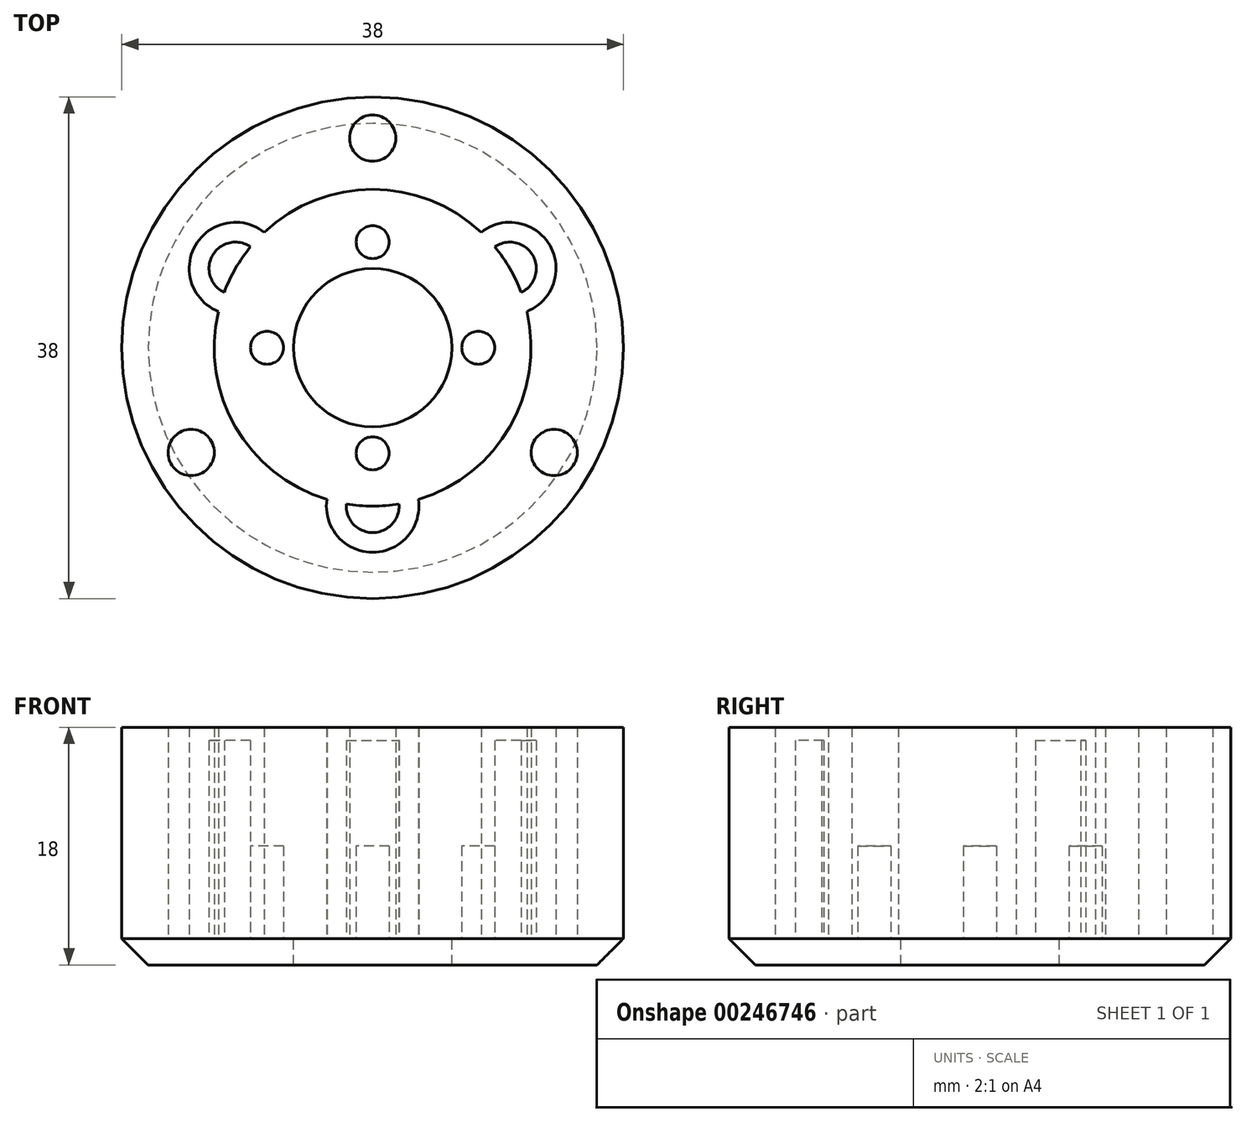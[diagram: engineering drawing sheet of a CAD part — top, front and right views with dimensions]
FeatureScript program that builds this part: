
annotation { "Feature Type Name" : "Feature", "Feature Type Description" : "" }
export const myFeature = defineFeature(function(context is Context, id is Id, definition is map)
    precondition{}
    {
        {
            var Q0;
            Q0=qCreatedBy(makeId("Top.planeOp"),FACE);
            var sketch = newSketch(context, id + "F0", { "sketchPlane" : qUnion([Q0])});
            skCircle(sketch, "E0", {"center": v(0, 0) * mm, "radius": 12 * mm});
            skCircle(sketch, "E1", {"center": v(0, 0) * mm, "radius": 8 * mm, "construction": true});
            skLineSegment(sketch, "E2", {"start": v(0, 34.6) * mm, "end": v(0, -37) * mm, "construction": true});
            skLineSegment(sketch, "E3", {"start": v(36.08, 20.83) * mm, "end": v(-44.46, -25.67) * mm, "construction": true});
            skLineSegment(sketch, "E4", {"start": v(-38.88, 22.45) * mm, "end": v(53.4, -30.83) * mm, "construction": true});
            skCircle(sketch, "E5", {"center": v(-10.4, 6) * mm, "radius": 3.5 * mm});
            skCircle(sketch, "E6", {"center": v(10.4, 6) * mm, "radius": 3.5 * mm});
            skCircle(sketch, "E7", {"center": v(0, -12) * mm, "radius": 3.5 * mm});
            skCircle(sketch, "E8", {"center": v(0, 0) * mm, "radius": 19 * mm});
            skCircle(sketch, "E9", {"center": v(0, 0) * mm, "radius": 15.88 * mm, "construction": true});
            skCircle(sketch, "E10", {"center": v(-13.75, -7.94) * mm, "radius": 1.75 * mm});
            skCircle(sketch, "E11", {"center": v(13.75, -7.94) * mm, "radius": 1.75 * mm});
            skCircle(sketch, "E12", {"center": v(0, 15.88) * mm, "radius": 1.75 * mm});
            skCircle(sketch, "E13", {"center": v(-10.4, 6) * mm, "radius": 2 * mm});
            skCircle(sketch, "E14", {"center": v(10.4, 6) * mm, "radius": 2 * mm});
            skCircle(sketch, "E15", {"center": v(0, -12) * mm, "radius": 2 * mm});
            skCircle(sketch, "E16", {"center": v(0, 0) * mm, "radius": 6 * mm});
            skCircle(sketch, "E17", {"center": v(0, 8) * mm, "radius": 1.25 * mm});
            skCircle(sketch, "E18", {"center": v(8, 0) * mm, "radius": 1.25 * mm});
            skCircle(sketch, "E19", {"center": v(-8, 0) * mm, "radius": 1.25 * mm});
            skCircle(sketch, "E20", {"center": v(0, -8) * mm, "radius": 1.25 * mm});
            skSolve(sketch);
        }
        {
            var Q0;
            Q0=makeQuery(id+"F0.imprint","IMPRINT",FACE,{"disambiguationData":[TD([[makeQuery(id+"F0.imprint","IMPRINT",EDGE,{"derivedFrom":sQuery(id+"F0.wireOp",EDGE,"E8")}),1.0]])]});
            extrude(context, id + "F1", {"entities" : qUnion([Q0]), "depth" : 16 * mm});
        }
        {
            var Q0;
            Q0=makeQuery(id+"F0.imprint","IMPRINT",FACE,{"disambiguationData":[TD([[makeQuery(id+"F0.imprint","IMPRINT",EDGE,{"derivedFrom":sQuery(id+"F0.wireOp",EDGE,"E10")}),1.0]])]});
            var Q1;
            {var subQ0=sQuery(id+"F0.wireOp",EDGE,"E14");var subQ1=sQuery(id+"F0.wireOp",EDGE,"E0");var subQ2=makeQuery(id+"F0.imprint","INTERSECT",VERTEX,{"disambiguationData":[OD(0.0)],"derivedFrom":[subQ1,subQ0]});Q1=makeQuery(id+"F0.imprint","IMPRINT",FACE,{"disambiguationData":[TD([[makeQuery(id+"F0.imprint","IMPRINT",EDGE,{"disambiguationData":[TD([[subQ2,1.0]])],"derivedFrom":subQ1}),-1.0]])]});}
            var Q2;
            {var subQ0=sQuery(id+"F0.wireOp",EDGE,"E14");var subQ1=sQuery(id+"F0.wireOp",EDGE,"E0");var subQ2=makeQuery(id+"F0.imprint","INTERSECT",VERTEX,{"disambiguationData":[OD(0.0)],"derivedFrom":[subQ1,subQ0]});Q2=makeQuery(id+"F0.imprint","IMPRINT",FACE,{"disambiguationData":[TD([[makeQuery(id+"F0.imprint","IMPRINT",EDGE,{"disambiguationData":[TD([[subQ2,1.0]])],"derivedFrom":subQ1}),1.0]])]});}
            var Q3;
            {var subQ0=sQuery(id+"F0.wireOp",EDGE,"E7");var subQ1=sQuery(id+"F0.wireOp",EDGE,"E0");var subQ7=makeQuery(id+"F0.imprint","INTERSECT",VERTEX,{"disambiguationData":[OD(0.0)],"derivedFrom":[subQ1,subQ0]});Q3=makeQuery(id+"F0.imprint","IMPRINT",FACE,{"disambiguationData":[TD([[makeQuery(id+"F0.imprint","IMPRINT",EDGE,{"disambiguationData":[TD([[subQ7,-1.0]])],"derivedFrom":subQ1}),1.0]])]});}
            var Q4;
            Q4=makeQuery(id+"F0.imprint","IMPRINT",FACE,{"disambiguationData":[TD([[makeQuery(id+"F0.imprint","IMPRINT",EDGE,{"derivedFrom":sQuery(id+"F0.wireOp",EDGE,"E16")}),-1.0]])]});
            var Q5;
            {var subQ0=sQuery(id+"F0.wireOp",EDGE,"E7");var subQ1=sQuery(id+"F0.wireOp",EDGE,"E0");var subQ2=makeQuery(id+"F0.imprint","INTERSECT",VERTEX,{"disambiguationData":[OD(0.0)],"derivedFrom":[subQ1,subQ0]});Q5=makeQuery(id+"F0.imprint","IMPRINT",FACE,{"disambiguationData":[TD([[makeQuery(id+"F0.imprint","IMPRINT",EDGE,{"disambiguationData":[TD([[subQ2,-1.0]])],"derivedFrom":subQ1}),-1.0]])]});}
            var Q6;
            Q6=makeQuery(id+"F0.imprint","IMPRINT",FACE,{"disambiguationData":[TD([[makeQuery(id+"F0.imprint","IMPRINT",EDGE,{"derivedFrom":sQuery(id+"F0.wireOp",EDGE,"E11")}),1.0]])]});
            var Q7;
            Q7=makeQuery(id+"F0.imprint","IMPRINT",FACE,{"disambiguationData":[TD([[makeQuery(id+"F0.imprint","IMPRINT",EDGE,{"derivedFrom":sQuery(id+"F0.wireOp",EDGE,"E12")}),1.0]])]});
            var Q8;
            {var subQ0=sQuery(id+"F0.wireOp",EDGE,"E14");var subQ1=sQuery(id+"F0.wireOp",EDGE,"E0");var subQ2=makeQuery(id+"F0.imprint","INTERSECT",VERTEX,{"disambiguationData":[OD(0.0)],"derivedFrom":[subQ1,subQ0]});Q8=makeQuery(id+"F0.imprint","IMPRINT",FACE,{"disambiguationData":[TD([[makeQuery(id+"F0.imprint","IMPRINT",EDGE,{"disambiguationData":[TD([[subQ2,-1.0]])],"derivedFrom":subQ1}),1.0]])]});}
            var Q9;
            {var subQ0=sQuery(id+"F0.wireOp",EDGE,"E14");var subQ1=sQuery(id+"F0.wireOp",EDGE,"E0");var subQ2=makeQuery(id+"F0.imprint","INTERSECT",VERTEX,{"disambiguationData":[OD(0.0)],"derivedFrom":[subQ1,subQ0]});Q9=makeQuery(id+"F0.imprint","IMPRINT",FACE,{"disambiguationData":[TD([[makeQuery(id+"F0.imprint","IMPRINT",EDGE,{"disambiguationData":[TD([[subQ2,-1.0]])],"derivedFrom":subQ1}),-1.0]])]});}
            var Q10;
            {var subQ0=sQuery(id+"F0.wireOp",EDGE,"E13");var subQ1=sQuery(id+"F0.wireOp",EDGE,"E0");var subQ2=makeQuery(id+"F0.imprint","INTERSECT",VERTEX,{"disambiguationData":[OD(0.0)],"derivedFrom":[subQ1,subQ0]});Q10=makeQuery(id+"F0.imprint","IMPRINT",FACE,{"disambiguationData":[TD([[makeQuery(id+"F0.imprint","IMPRINT",EDGE,{"disambiguationData":[TD([[subQ2,-1.0]])],"derivedFrom":subQ1}),-1.0]])]});}
            var Q11;
            {var subQ0=sQuery(id+"F0.wireOp",EDGE,"E13");var subQ1=sQuery(id+"F0.wireOp",EDGE,"E0");var subQ2=makeQuery(id+"F0.imprint","INTERSECT",VERTEX,{"disambiguationData":[OD(0.0)],"derivedFrom":[subQ1,subQ0]});Q11=makeQuery(id+"F0.imprint","IMPRINT",FACE,{"disambiguationData":[TD([[makeQuery(id+"F0.imprint","IMPRINT",EDGE,{"disambiguationData":[TD([[subQ2,-1.0]])],"derivedFrom":subQ1}),1.0]])]});}
            var Q12;
            {var subQ0=sQuery(id+"F0.wireOp",EDGE,"E15");var subQ1=sQuery(id+"F0.wireOp",EDGE,"E0");var subQ2=makeQuery(id+"F0.imprint","INTERSECT",VERTEX,{"disambiguationData":[OD(0.0)],"derivedFrom":[subQ1,subQ0]});Q12=makeQuery(id+"F0.imprint","IMPRINT",FACE,{"disambiguationData":[TD([[makeQuery(id+"F0.imprint","IMPRINT",EDGE,{"disambiguationData":[TD([[subQ2,-1.0]])],"derivedFrom":subQ1}),1.0]])]});}
            var Q13;
            {var subQ0=sQuery(id+"F0.wireOp",EDGE,"E15");var subQ1=sQuery(id+"F0.wireOp",EDGE,"E0");var subQ2=makeQuery(id+"F0.imprint","INTERSECT",VERTEX,{"disambiguationData":[OD(0.0)],"derivedFrom":[subQ1,subQ0]});Q13=makeQuery(id+"F0.imprint","IMPRINT",FACE,{"disambiguationData":[TD([[makeQuery(id+"F0.imprint","IMPRINT",EDGE,{"disambiguationData":[TD([[subQ2,-1.0]])],"derivedFrom":subQ1}),-1.0]])]});}
            var Q14;
            Q14=makeQuery(id+"F0.imprint","IMPRINT",FACE,{"disambiguationData":[TD([[makeQuery(id+"F0.imprint","IMPRINT",EDGE,{"derivedFrom":sQuery(id+"F0.wireOp",EDGE,"E8")}),1.0]])]});
            var Q15;
            {var subQ0=sQuery(id+"F0.wireOp",EDGE,"E5");var subQ1=sQuery(id+"F0.wireOp",EDGE,"E0");var subQ2=makeQuery(id+"F0.imprint","INTERSECT",VERTEX,{"disambiguationData":[OD(0.0)],"derivedFrom":[subQ1,subQ0]});Q15=makeQuery(id+"F0.imprint","IMPRINT",FACE,{"disambiguationData":[TD([[makeQuery(id+"F0.imprint","IMPRINT",EDGE,{"disambiguationData":[TD([[subQ2,-1.0]])],"derivedFrom":subQ1}),-1.0]])]});}
            var Q16;
            {var subQ0=sQuery(id+"F0.wireOp",EDGE,"E5");var subQ1=sQuery(id+"F0.wireOp",EDGE,"E0");var subQ2=makeQuery(id+"F0.imprint","INTERSECT",VERTEX,{"disambiguationData":[OD(0.0)],"derivedFrom":[subQ1,subQ0]});Q16=makeQuery(id+"F0.imprint","IMPRINT",FACE,{"disambiguationData":[TD([[makeQuery(id+"F0.imprint","IMPRINT",EDGE,{"disambiguationData":[TD([[subQ2,-1.0]])],"derivedFrom":subQ1}),1.0]])]});}
            var Q17;
            Q17=makeQuery(id+"F1.opExtrude","CAP_FACE",FACE,{"disambiguationData":[OSD([sQuery(id+"F0.wireOp",EDGE,"E0"),sQuery(id+"F0.wireOp",EDGE,"E5"),sQuery(id+"F0.wireOp",EDGE,"E6"),sQuery(id+"F0.wireOp",EDGE,"E7"),sQuery(id+"F0.wireOp",EDGE,"E8"),sQuery(id+"F0.wireOp",EDGE,"E10"),sQuery(id+"F0.wireOp",EDGE,"E11"),sQuery(id+"F0.wireOp",EDGE,"E12")])],"isStart":true});
            var Q18;
            {var subQ0=sQuery(id+"F0.wireOp",EDGE,"E20");var subQ1=sQuery(id+"F0.wireOp",EDGE,"E7");var subQ2=makeQuery(id+"F0.imprint","INTERSECT",VERTEX,{"disambiguationData":[OD(0.0)],"derivedFrom":[subQ1,subQ0]});Q18=makeQuery(id+"F0.imprint","IMPRINT",FACE,{"disambiguationData":[TD([[makeQuery(id+"F0.imprint","IMPRINT",EDGE,{"disambiguationData":[TD([[subQ2,-1.0]])],"derivedFrom":subQ1}),-1.0]])]});}
            var Q19;
            Q19=makeQuery(id+"F0.imprint","IMPRINT",FACE,{"disambiguationData":[TD([[makeQuery(id+"F0.imprint","IMPRINT",EDGE,{"derivedFrom":sQuery(id+"F0.wireOp",EDGE,"E17")}),1.0]])]});
            var Q20;
            Q20=makeQuery(id+"F0.imprint","IMPRINT",FACE,{"disambiguationData":[TD([[makeQuery(id+"F0.imprint","IMPRINT",EDGE,{"derivedFrom":sQuery(id+"F0.wireOp",EDGE,"E18")}),1.0]])]});
            var Q21;
            Q21=makeQuery(id+"F0.imprint","IMPRINT",FACE,{"disambiguationData":[TD([[makeQuery(id+"F0.imprint","IMPRINT",EDGE,{"derivedFrom":sQuery(id+"F0.wireOp",EDGE,"E19")}),1.0]])]});
            var Q22;
            Q22=makeQuery(id+"F1.opExtrude","CAP_FACE",FACE,{"disambiguationData":[OSD([sQuery(id+"F0.wireOp",EDGE,"E0"),sQuery(id+"F0.wireOp",EDGE,"E5"),sQuery(id+"F0.wireOp",EDGE,"E6"),sQuery(id+"F0.wireOp",EDGE,"E7"),sQuery(id+"F0.wireOp",EDGE,"E8"),sQuery(id+"F0.wireOp",EDGE,"E10"),sQuery(id+"F0.wireOp",EDGE,"E11"),sQuery(id+"F0.wireOp",EDGE,"E12")])],"isStart":false});
            var Q23;
            {var subQ0=sQuery(id+"F0.wireOp",EDGE,"E20");var subQ1=sQuery(id+"F0.wireOp",EDGE,"E7");var subQ2=makeQuery(id+"F0.imprint","INTERSECT",VERTEX,{"disambiguationData":[OD(0.0)],"derivedFrom":[subQ1,subQ0]});Q23=makeQuery(id+"F0.imprint","IMPRINT",FACE,{"disambiguationData":[TD([[makeQuery(id+"F0.imprint","IMPRINT",EDGE,{"disambiguationData":[TD([[subQ2,-1.0]])],"derivedFrom":subQ1}),1.0]])]});}
            extrude(context, id + "F2", {"entities" : qUnion([Q0, Q1, Q2, Q3, Q4, Q5, Q6, Q7, Q8, Q9, Q10, Q11, Q12, Q13, Q14, Q15, Q16, Q17, Q18, Q19, Q20, Q21, Q22, Q23]), "operationType" : NewBodyOperationType.ADD, "oppositeDirection" : true, "depth" : 2 * mm});
        }
        {
            var Q0;
            Q0=makeQuery(id+"F0.imprint","IMPRINT",FACE,{"disambiguationData":[TD([[makeQuery(id+"F0.imprint","IMPRINT",EDGE,{"derivedFrom":sQuery(id+"F0.wireOp",EDGE,"E19")}),1.0]])]});
            var Q1;
            Q1=makeQuery(id+"F0.imprint","IMPRINT",FACE,{"disambiguationData":[TD([[makeQuery(id+"F0.imprint","IMPRINT",EDGE,{"derivedFrom":sQuery(id+"F0.wireOp",EDGE,"E17")}),1.0]])]});
            var Q2;
            Q2=makeQuery(id+"F0.imprint","IMPRINT",FACE,{"disambiguationData":[TD([[makeQuery(id+"F0.imprint","IMPRINT",EDGE,{"derivedFrom":sQuery(id+"F0.wireOp",EDGE,"E18")}),1.0]])]});
            var Q3;
            {var subQ0=sQuery(id+"F0.wireOp",EDGE,"E20");var subQ1=sQuery(id+"F0.wireOp",EDGE,"E7");var subQ2=makeQuery(id+"F0.imprint","INTERSECT",VERTEX,{"disambiguationData":[OD(0.0)],"derivedFrom":[subQ1,subQ0]});Q3=makeQuery(id+"F0.imprint","IMPRINT",FACE,{"disambiguationData":[TD([[makeQuery(id+"F0.imprint","IMPRINT",EDGE,{"disambiguationData":[TD([[subQ2,-1.0]])],"derivedFrom":subQ1}),-1.0]])]});}
            var Q4;
            {var subQ0=sQuery(id+"F0.wireOp",EDGE,"E20");var subQ1=sQuery(id+"F0.wireOp",EDGE,"E7");var subQ2=makeQuery(id+"F0.imprint","INTERSECT",VERTEX,{"disambiguationData":[OD(0.0)],"derivedFrom":[subQ1,subQ0]});Q4=makeQuery(id+"F0.imprint","IMPRINT",FACE,{"disambiguationData":[TD([[makeQuery(id+"F0.imprint","IMPRINT",EDGE,{"disambiguationData":[TD([[subQ2,-1.0]])],"derivedFrom":subQ1}),1.0]])]});}
            var Q5;
            Q5=sQuery(id+"F0.wireOp",EDGE,"mDgNqodb-BoqN-Pv4V-Kohz-QChm2wdieeZA");
            var Q6;
            Q6=sQuery(id+"F0.wireOp",EDGE,"3FOjPB5A-skdb-4wiH-Bc0L-Vw7G0X0bc6KK");
            var Q7;
            Q7=sQuery(id+"F0.wireOp",EDGE,"7GB3At82-350K-cK2M-76G1-KneQQoefS5Zi");
            var Q8;
            Q8=sQuery(id+"F0.wireOp",EDGE,"JW66KMjt-9Xx5-beP8-O577-gAs5ANOXeLvY");
            extrude(context, id + "F3", {"entities" : qUnion([Q0, Q1, Q2, Q3, Q4]), "operationType" : NewBodyOperationType.ADD, "surfaceEntities" : qUnion([Q5, Q6, Q7, Q8]), "depth" : 7 * mm});
        }
        {
            var Q0;
            {var subQ0=sQuery(id+"F0.wireOp",EDGE,"E8");Q0=makeQuery(id+"F2.opExtrude","CAP_EDGE",EDGE,{"disambiguationData":[OSD([subQ0]),TDD([makeQuery(id+"F0.imprint","IMPRINT",EDGE,{"derivedFrom":subQ0})])],"isStart":false});}
            chamfer(context, id + "F4", {"entities" : qUnion([Q0]), "width" : 2 * mm, "tangentPropagation" : true});
        }
        {
            var Q0;
            {var subQ0=sQuery(id+"F0.wireOp",EDGE,"E13");var subQ1=sQuery(id+"F0.wireOp",EDGE,"E0");var subQ2=makeQuery(id+"F0.imprint","INTERSECT",VERTEX,{"disambiguationData":[OD(0.0)],"derivedFrom":[subQ1,subQ0]});Q0=makeQuery(id+"F0.imprint","IMPRINT",FACE,{"disambiguationData":[TD([[makeQuery(id+"F0.imprint","IMPRINT",EDGE,{"disambiguationData":[TD([[subQ2,-1.0]])],"derivedFrom":subQ1}),-1.0]])]});}
            var Q1;
            {var subQ0=sQuery(id+"F0.wireOp",EDGE,"E14");var subQ1=sQuery(id+"F0.wireOp",EDGE,"E0");var subQ2=makeQuery(id+"F0.imprint","INTERSECT",VERTEX,{"disambiguationData":[OD(0.0)],"derivedFrom":[subQ1,subQ0]});Q1=makeQuery(id+"F0.imprint","IMPRINT",FACE,{"disambiguationData":[TD([[makeQuery(id+"F0.imprint","IMPRINT",EDGE,{"disambiguationData":[TD([[subQ2,-1.0]])],"derivedFrom":subQ1}),-1.0]])]});}
            var Q2;
            {var subQ0=sQuery(id+"F0.wireOp",EDGE,"E15");var subQ1=sQuery(id+"F0.wireOp",EDGE,"E0");var subQ2=makeQuery(id+"F0.imprint","INTERSECT",VERTEX,{"disambiguationData":[OD(0.0)],"derivedFrom":[subQ1,subQ0]});Q2=makeQuery(id+"F0.imprint","IMPRINT",FACE,{"disambiguationData":[TD([[makeQuery(id+"F0.imprint","IMPRINT",EDGE,{"disambiguationData":[TD([[subQ2,-1.0]])],"derivedFrom":subQ1}),-1.0]])]});}
            extrude(context, id + "F5", {"entities" : qUnion([Q0, Q1, Q2]), "operationType" : NewBodyOperationType.ADD, "depth" : 15 * mm});
        }
    });
